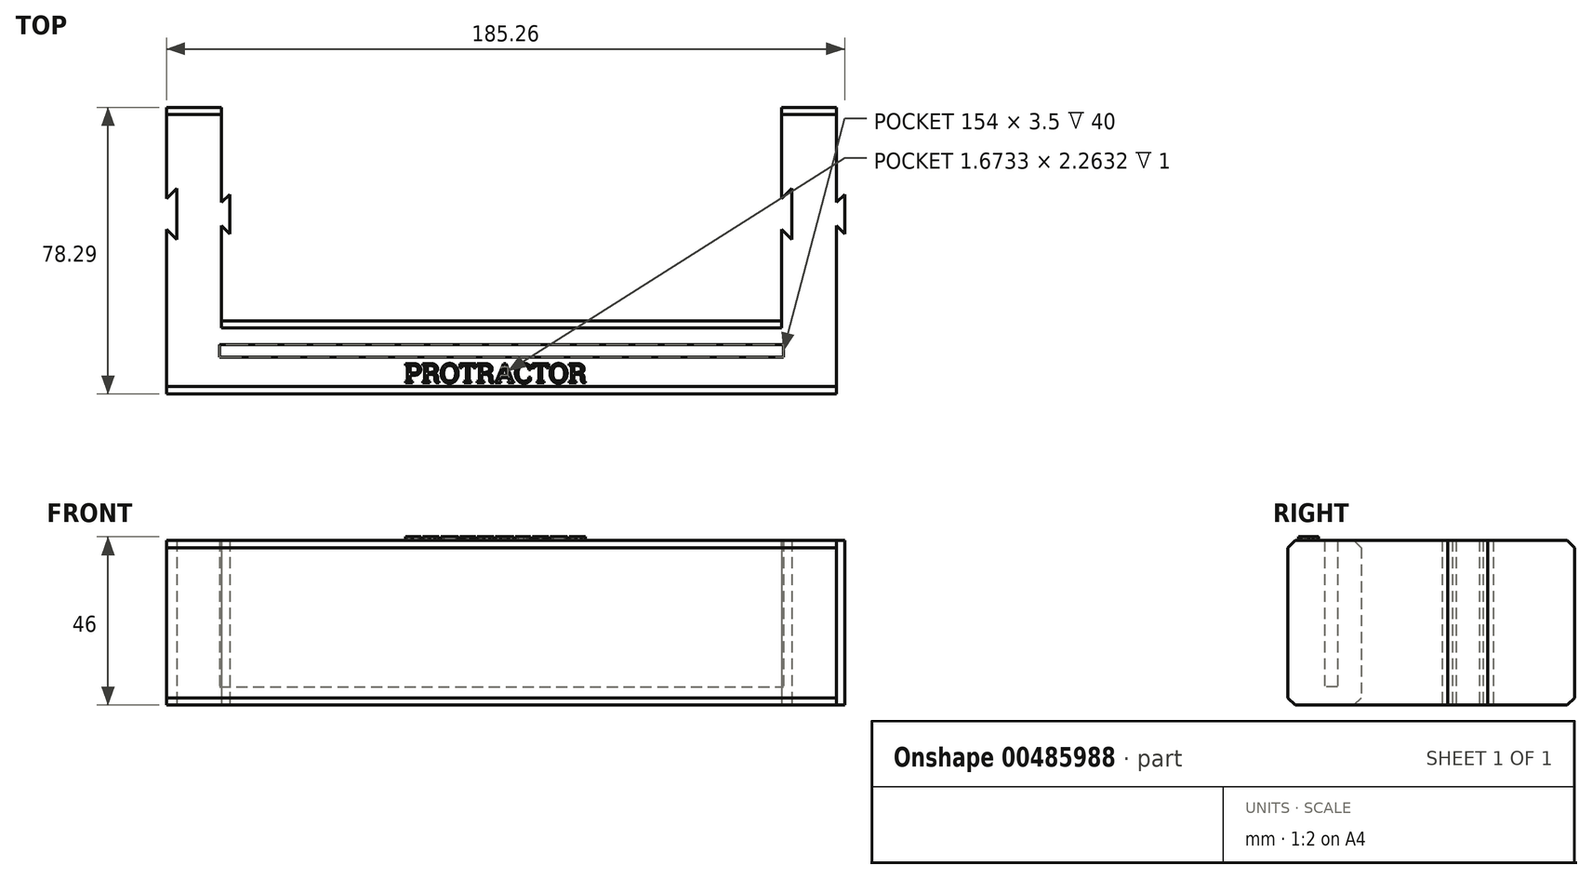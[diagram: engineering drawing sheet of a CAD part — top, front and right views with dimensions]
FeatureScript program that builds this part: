
annotation { "Feature Type Name" : "Feature", "Feature Type Description" : "" }
export const myFeature = defineFeature(function(context is Context, id is Id, definition is map)
    precondition{}
    {
        {
            var Q0;
            Q0=qCreatedBy(makeId("Top.planeOp"),FACE);
            var sketch = newSketch(context, id + "F0", { "sketchPlane" : qUnion([Q0])});
            skLineSegment(sketch, "E0", {"start": v(-15, 4.17) * mm, "end": v(-15, 29.17) * mm});
            skLineSegment(sketch, "E1", {"start": v(-15, 29.17) * mm, "end": v(0, 29.17) * mm});
            skLineSegment(sketch, "E2", {"start": v(0, 29.17) * mm, "end": v(0, 3.17) * mm});
            skLineSegment(sketch, "E3", {"start": v(-15, 4.17) * mm, "end": v(-12.17, 7) * mm});
            skLineSegment(sketch, "E4", {"start": v(-12.17, 7) * mm, "end": v(-12.17, 0) * mm});
            skLineSegment(sketch, "E5", {"start": v(0, 3.17) * mm, "end": v(2.26, 5.43) * mm});
            skLineSegment(sketch, "E6", {"start": v(2.26, 5.43) * mm, "end": v(2.26, -0.57) * mm});
            skLineSegment(sketch, "E7.MirrorCS", {"start": v(-15, -4.12) * mm, "end": v(-12.17, -6.95) * mm});
            skLineSegment(sketch, "E8.MirrorCS", {"start": v(0, -29.12) * mm, "end": v(0, -3.12) * mm});
            skLineSegment(sketch, "E9.MirrorCS", {"start": v(-12.17, -6.95) * mm, "end": v(-12.17, 0.05) * mm});
            skLineSegment(sketch, "E10.MirrorCS", {"start": v(-15, -4.12) * mm, "end": v(-15, -29.12) * mm});
            skLineSegment(sketch, "E11.MirrorCS", {"start": v(2.26, -5.39) * mm, "end": v(2.26, 0.61) * mm});
            skLineSegment(sketch, "E12.MirrorCS", {"start": v(0, -3.12) * mm, "end": v(2.26, -5.39) * mm});
            skLineSegment(sketch, "E13", {"start": v(153, 4.17) * mm, "end": v(153, 29.17) * mm});
            skLineSegment(sketch, "E14", {"start": v(153, 29.17) * mm, "end": v(168, 29.17) * mm});
            skLineSegment(sketch, "E15", {"start": v(168, 29.17) * mm, "end": v(168, 3.17) * mm});
            skLineSegment(sketch, "E16", {"start": v(153, 4.17) * mm, "end": v(155.83, 7) * mm});
            skLineSegment(sketch, "E17", {"start": v(155.83, 7) * mm, "end": v(155.83, 0) * mm});
            skLineSegment(sketch, "E18", {"start": v(168, 3.17) * mm, "end": v(170.26, 5.43) * mm});
            skLineSegment(sketch, "E19", {"start": v(170.26, 5.43) * mm, "end": v(170.26, -0.57) * mm});
            skLineSegment(sketch, "E20.MirrorCS", {"start": v(153, -4.17) * mm, "end": v(155.83, -7) * mm});
            skLineSegment(sketch, "E21.MirrorCS", {"start": v(168, -29.17) * mm, "end": v(168, -3.17) * mm});
            skLineSegment(sketch, "E22.MirrorCS", {"start": v(155.83, -7) * mm, "end": v(155.83, 0) * mm});
            skLineSegment(sketch, "E23.MirrorCS", {"start": v(153, -4.17) * mm, "end": v(153, -29.17) * mm});
            skLineSegment(sketch, "E24.MirrorCS", {"start": v(170.26, -5.43) * mm, "end": v(170.26, 0.57) * mm});
            skLineSegment(sketch, "E25.MirrorCS", {"start": v(168, -3.17) * mm, "end": v(170.26, -5.43) * mm});
            skLineSegment(sketch, "E26.bottom", {"start": v(-15, -29.12) * mm, "end": v(168, -29.12) * mm});
            skLineSegment(sketch, "E26.top", {"start": v(-15, -49.12) * mm, "end": v(168, -49.12) * mm});
            skLineSegment(sketch, "E26.left", {"start": v(-15, -29.12) * mm, "end": v(-15, -49.12) * mm});
            skLineSegment(sketch, "E26.right", {"start": v(168, -29.12) * mm, "end": v(168, -49.12) * mm});
            skLineSegment(sketch, "E27.bottom", {"start": v(-0.5, -35.62) * mm, "end": v(153.5, -35.62) * mm});
            skLineSegment(sketch, "E27.top", {"start": v(-0.5, -39.12) * mm, "end": v(153.5, -39.12) * mm});
            skLineSegment(sketch, "E27.left", {"start": v(-0.5, -35.62) * mm, "end": v(-0.5, -39.12) * mm});
            skLineSegment(sketch, "E27.right", {"start": v(153.5, -35.62) * mm, "end": v(153.5, -39.12) * mm});
            skSolve(sketch);
        }
        {
            var Q0;
            Q0=qSketchRegion(id+"F0",true);
            extrude(context, id + "F1", {"entities" : qUnion([Q0]), "depth" : 40 * mm});
        }
        {
            var Q0;
            Q0=makeQuery(id+"F0.imprint","IMPRINT",FACE,{"disambiguationData":[TD([[makeQuery(id+"F0.imprint","IMPRINT",EDGE,{"derivedFrom":sQuery(id+"F0.wireOp",EDGE,"E0")}),-1.0]])]});
            var Q1;
            Q1=makeQuery(id+"F0.imprint","IMPRINT",FACE,{"disambiguationData":[TD([[makeQuery(id+"F0.imprint","IMPRINT",EDGE,{"derivedFrom":sQuery(id+"F0.wireOp",EDGE,"E13")}),-1.0]])]});
            var Q2;
            Q2=makeQuery(id+"F0.imprint","IMPRINT",FACE,{"disambiguationData":[TD([[makeQuery(id+"F0.imprint","IMPRINT",EDGE,{"derivedFrom":sQuery(id+"F0.wireOp",EDGE,"E27.bottom")}),-1.0]])]});
            var Q3;
            {var subQ0=sQuery(id+"F0.wireOp",EDGE,"E26.top");Q3=makeQuery(id+"F0.imprint","IMPRINT",FACE,{"disambiguationData":[TD([[makeQuery(id+"F0.imprint","IMPRINT",EDGE,{"derivedFrom":subQ0}),1.0]])]});}
            extrude(context, id + "F2", {"entities" : qUnion([Q0, Q1, Q2, Q3]), "operationType" : NewBodyOperationType.ADD, "oppositeDirection" : true, "depth" : 5 * mm});
        }
        {
            var Q0;
            Q0=makeQuery(id+"F1.opExtrude","CAP_FACE",FACE,{"disambiguationData":[OSD([sQuery(id+"F0.wireOp",EDGE,"E0"),sQuery(id+"F0.wireOp",EDGE,"E1"),sQuery(id+"F0.wireOp",EDGE,"E2"),sQuery(id+"F0.wireOp",EDGE,"E3"),sQuery(id+"F0.wireOp",EDGE,"E4"),sQuery(id+"F0.wireOp",EDGE,"E5"),sQuery(id+"F0.wireOp",EDGE,"E6"),sQuery(id+"F0.wireOp",EDGE,"E7.MirrorCS"),sQuery(id+"F0.wireOp",EDGE,"E8.MirrorCS"),sQuery(id+"F0.wireOp",EDGE,"E9.MirrorCS"),sQuery(id+"F0.wireOp",EDGE,"E10.MirrorCS"),sQuery(id+"F0.wireOp",EDGE,"E11.MirrorCS"),sQuery(id+"F0.wireOp",EDGE,"E12.MirrorCS"),sQuery(id+"F0.wireOp",EDGE,"4d0a05fa-104b-468e-bad1-6da2c3376b846.MirrorCS"),sQuery(id+"F0.wireOp",EDGE,"KJNpoHbQ-aakG-BKsl-bdhx-CXvc9NHGIqeu.bottom"),sQuery(id+"F0.wireOp",EDGE,"KJNpoHbQ-aakG-BKsl-bdhx-CXvc9NHGIqeu.top"),sQuery(id+"F0.wireOp",EDGE,"KJNpoHbQ-aakG-BKsl-bdhx-CXvc9NHGIqeu.left"),sQuery(id+"F0.wireOp",EDGE,"KJNpoHbQ-aakG-BKsl-bdhx-CXvc9NHGIqeu.right")])],"isStart":false});
            var sketch = newSketch(context, id + "F3", { "sketchPlane" : qUnion([Q0])});
            skText(sketch, "E28", { "text": "PROTRACTOR", "fontName": "RobotoSlab-Regular.ttf"});
            const initialGuessF3  = {"E28": [0.05, -0.04612, 1, 0, 0.00534]};
            skSetInitialGuess(sketch, initialGuessF3);
            skSolve(sketch);
        }
        {
            var Q0;
            Q0=qSketchRegion(id+"F3",true);
            extrude(context, id + "F4", {"entities" : qUnion([Q0]), "operationType" : NewBodyOperationType.ADD, "depth" : 1 * mm});
        }
        {
            var Q0;
            Q0=makeQuery(id+"F1.opExtrude","CAP_EDGE",EDGE,{"disambiguationData":[OSD([sQuery(id+"F0.wireOp",EDGE,"E26.top")])],"isStart":false});
            var Q1;
            Q1=makeQuery(id+"F1.opExtrude","CAP_EDGE",EDGE,{"disambiguationData":[OSD([sQuery(id+"F0.wireOp",EDGE,"E1")])],"isStart":false});
            var Q2;
            Q2=makeQuery(id+"F1.opExtrude","CAP_EDGE",EDGE,{"disambiguationData":[OSD([sQuery(id+"F0.wireOp",EDGE,"E14")])],"isStart":false});
            var Q3;
            Q3=makeQuery(id+"F1.opExtrude","CAP_EDGE",EDGE,{"disambiguationData":[OSD([sQuery(id+"F0.wireOp",EDGE,"E26.bottom")])],"isStart":false});
            var Q4;
            Q4=makeQuery(id+"F2.opExtrude","CAP_EDGE",EDGE,{"disambiguationData":[OSD([sQuery(id+"F0.wireOp",EDGE,"E26.top")])],"isStart":false});
            var Q5;
            Q5=makeQuery(id+"F2.opExtrude","CAP_EDGE",EDGE,{"disambiguationData":[OSD([sQuery(id+"F0.wireOp",EDGE,"E26.bottom")])],"isStart":false});
            var Q6;
            Q6=makeQuery(id+"F2.opExtrude","CAP_EDGE",EDGE,{"disambiguationData":[OSD([sQuery(id+"F0.wireOp",EDGE,"E14")])],"isStart":false});
            var Q7;
            Q7=makeQuery(id+"F2.opExtrude","CAP_EDGE",EDGE,{"disambiguationData":[OSD([sQuery(id+"F0.wireOp",EDGE,"E1")])],"isStart":false});
            chamfer(context, id + "F5", {"entities" : qUnion([Q0, Q1, Q2, Q3, Q4, Q5, Q6, Q7]), "width" : 2 * mm, "tangentPropagation" : true});
        }
    });
